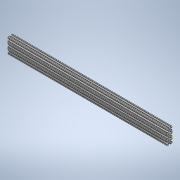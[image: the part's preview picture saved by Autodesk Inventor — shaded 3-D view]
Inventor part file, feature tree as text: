
AUTODESK INVENTOR PART (.ipt)
format: ipt  version: 2020 (Build 240168000, 168)  size: 390,144 bytes
history: native  units: in
note: dims shown in document units (in); Inventor stores cm internally (conversion verified against a paired STEP export)
features: sketch x2, extrude x1
ambient origin geometry x8: Origin, YZ Plane, XZ Plane, XY Plane, X Axis, Y Axis, Z Axis, Center Point
bodies: Solid1 (feature_tree)
feature tree (3):
  extrude  "Extrusion1"  [1 undecoded]
  sketch  "Sketch2"
  sketch  "Sketch1"  dims[d0=31.0in d1=0.0in]
note: 1 required parameter value undecoded (feature->parameter linkage not recoverable at this tier; creation-order binding heuristic only, values carry confidence <= 0.55)
